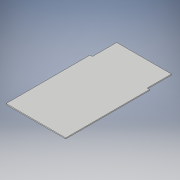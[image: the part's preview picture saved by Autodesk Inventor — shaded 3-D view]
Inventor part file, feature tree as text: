
AUTODESK INVENTOR PART (.ipt)
format: ipt  version: 2018 (Build 220112000, 112)  size: 97,792 bytes
history: native  units: in
note: dims shown in document units (in); Inventor stores cm internally (conversion verified against a paired STEP export)
features: extrude x1, sketch x1
ambient origin geometry x8: Origin, YZ Plane, XZ Plane, XY Plane, X Axis, Y Axis, Z Axis, Center Point
bodies: Solid1 (feature_tree)
feature tree (2):
  extrude  "Extrusion1"  Depth=2.7165in
  sketch  "Sketch1"  dims[d0=1.9291in d1=2.7165in d2=1.7717in d3=1.5748in d4=0.031in d5=0.0in]
